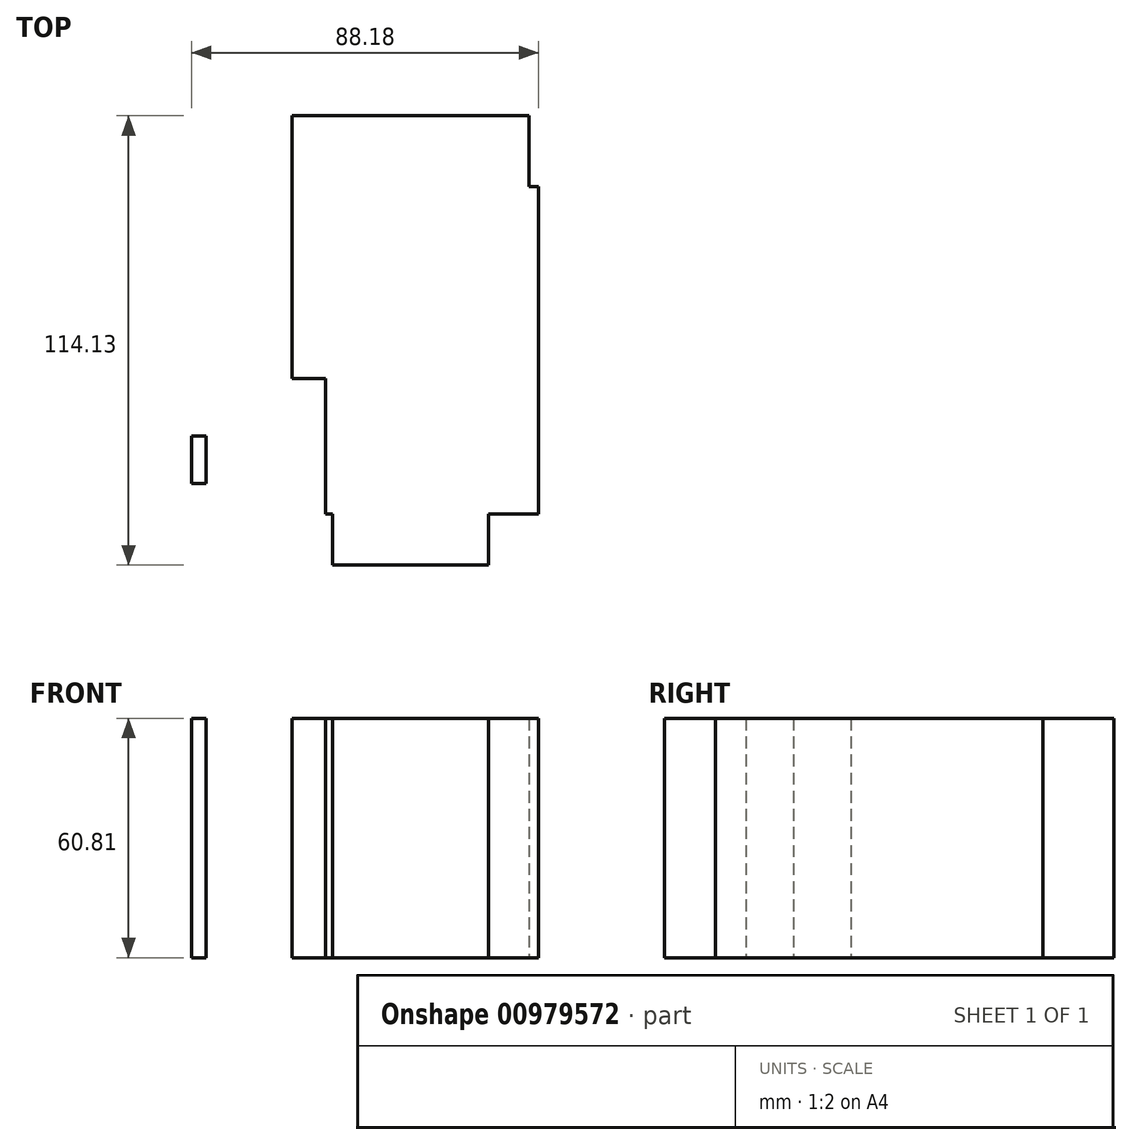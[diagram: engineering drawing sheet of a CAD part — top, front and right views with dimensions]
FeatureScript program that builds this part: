
annotation { "Feature Type Name" : "Feature", "Feature Type Description" : "" }
export const myFeature = defineFeature(function(context is Context, id is Id, definition is map)
    precondition{}
    {
        {
            var Q0;
            Q0=qCreatedBy(makeId("Top.planeOp"),FACE);
            var sketch = newSketch(context, id + "F0", { "sketchPlane" : qUnion([Q0])});
            skLineSegment(sketch, "E0.bottom", {"start": v(-50.4, -27.45) * mm, "end": v(-46.64, -27.45) * mm});
            skLineSegment(sketch, "E0.top", {"start": v(-50.4, -39.44) * mm, "end": v(-46.64, -39.44) * mm});
            skLineSegment(sketch, "E0.left", {"start": v(-50.4, -27.45) * mm, "end": v(-50.4, -39.44) * mm});
            skLineSegment(sketch, "E0.right", {"start": v(-46.64, -27.45) * mm, "end": v(-46.64, -39.44) * mm});
            skLineSegment(sketch, "E1.bottom", {"start": v(-38.1, -22.95) * mm, "end": v(-31.65, -22.95) * mm});
            skLineSegment(sketch, "E1.top", {"start": v(-38.1, -22.8) * mm, "end": v(-31.65, -22.8) * mm});
            skLineSegment(sketch, "E1.left", {"start": v(-38.1, -22.95) * mm, "end": v(-38.1, -22.8) * mm});
            skLineSegment(sketch, "E1.right", {"start": v(-31.65, -22.95) * mm, "end": v(-31.65, -22.8) * mm});
            skLineSegment(sketch, "E2.bottom", {"start": v(-24.9, -12.75) * mm, "end": v(35.4, -12.75) * mm});
            skLineSegment(sketch, "E2.top", {"start": v(-24.9, 54) * mm, "end": v(35.4, 54) * mm});
            skLineSegment(sketch, "E2.left", {"start": v(-24.9, -12.75) * mm, "end": v(-24.9, 54) * mm});
            skLineSegment(sketch, "E2.right", {"start": v(35.4, -12.75) * mm, "end": v(35.4, 54) * mm});
            skLineSegment(sketch, "E3.bottom", {"start": v(37.8, 36) * mm, "end": v(-16.35, 36) * mm});
            skLineSegment(sketch, "E3.top", {"start": v(37.8, -47.24) * mm, "end": v(-16.35, -47.24) * mm});
            skLineSegment(sketch, "E3.left", {"start": v(37.8, 36) * mm, "end": v(37.8, -47.24) * mm});
            skLineSegment(sketch, "E3.right", {"start": v(-16.35, 36) * mm, "end": v(-16.35, -47.24) * mm});
            skLineSegment(sketch, "E4.bottom", {"start": v(-14.55, -60.14) * mm, "end": v(25, -60.14) * mm});
            skLineSegment(sketch, "E4.top", {"start": v(-14.55, -47.24) * mm, "end": v(25, -47.24) * mm});
            skLineSegment(sketch, "E4.left", {"start": v(-14.55, -60.14) * mm, "end": v(-14.55, -47.24) * mm});
            skLineSegment(sketch, "E4.right", {"start": v(25, -60.14) * mm, "end": v(25, -47.24) * mm});
            skSolve(sketch);
        }
        {
            var Q0;
            {var subQ0=sQuery(id+"F0.wireOp",EDGE,"E3.left");Q0=makeQuery(id+"F0.imprint","IMPRINT",FACE,{"disambiguationData":[TD([[makeQuery(id+"F0.imprint","IMPRINT",EDGE,{"derivedFrom":subQ0}),-1.0]])]});}
            var Q1;
            Q1=makeQuery(id+"F0.imprint","IMPRINT",FACE,{"disambiguationData":[TD([[makeQuery(id+"F0.imprint","IMPRINT",EDGE,{"derivedFrom":sQuery(id+"F0.wireOp",EDGE,"E4.bottom")}),1.0]])]});
            var Q2;
            {var subQ1=sQuery(id+"F0.wireOp",EDGE,"E2.top");Q2=makeQuery(id+"F0.imprint","IMPRINT",FACE,{"disambiguationData":[TD([[makeQuery(id+"F0.imprint","IMPRINT",EDGE,{"derivedFrom":subQ1}),-1.0]])]});}
            var Q3;
            {var subQ0=sQuery(id+"F0.wireOp",EDGE,"E2.right");var subQ1=sQuery(id+"F0.wireOp",EDGE,"E2.bottom");var subQ2=makeQuery(id+"F0.imprint","INTERSECT",VERTEX,{"derivedFrom":[subQ1,subQ0]});Q3=makeQuery(id+"F0.imprint","IMPRINT",FACE,{"disambiguationData":[TD([[makeQuery(id+"F0.imprint","IMPRINT",EDGE,{"disambiguationData":[TD([[subQ2,1.0]])],"derivedFrom":subQ1}),1.0]])]});}
            var Q4;
            Q4=makeQuery(id+"F0.imprint","IMPRINT",FACE,{"disambiguationData":[TD([[makeQuery(id+"F0.imprint","IMPRINT",EDGE,{"derivedFrom":sQuery(id+"F0.wireOp",EDGE,"E0.bottom")}),-1.0]])]});
            extrude(context, id + "F1", {"entities" : qUnion([Q0, Q1, Q2, Q3, Q4]), "depth" : 60.8 * mm, "offsetDistance" : 25.4 * mm});
        }
    });
